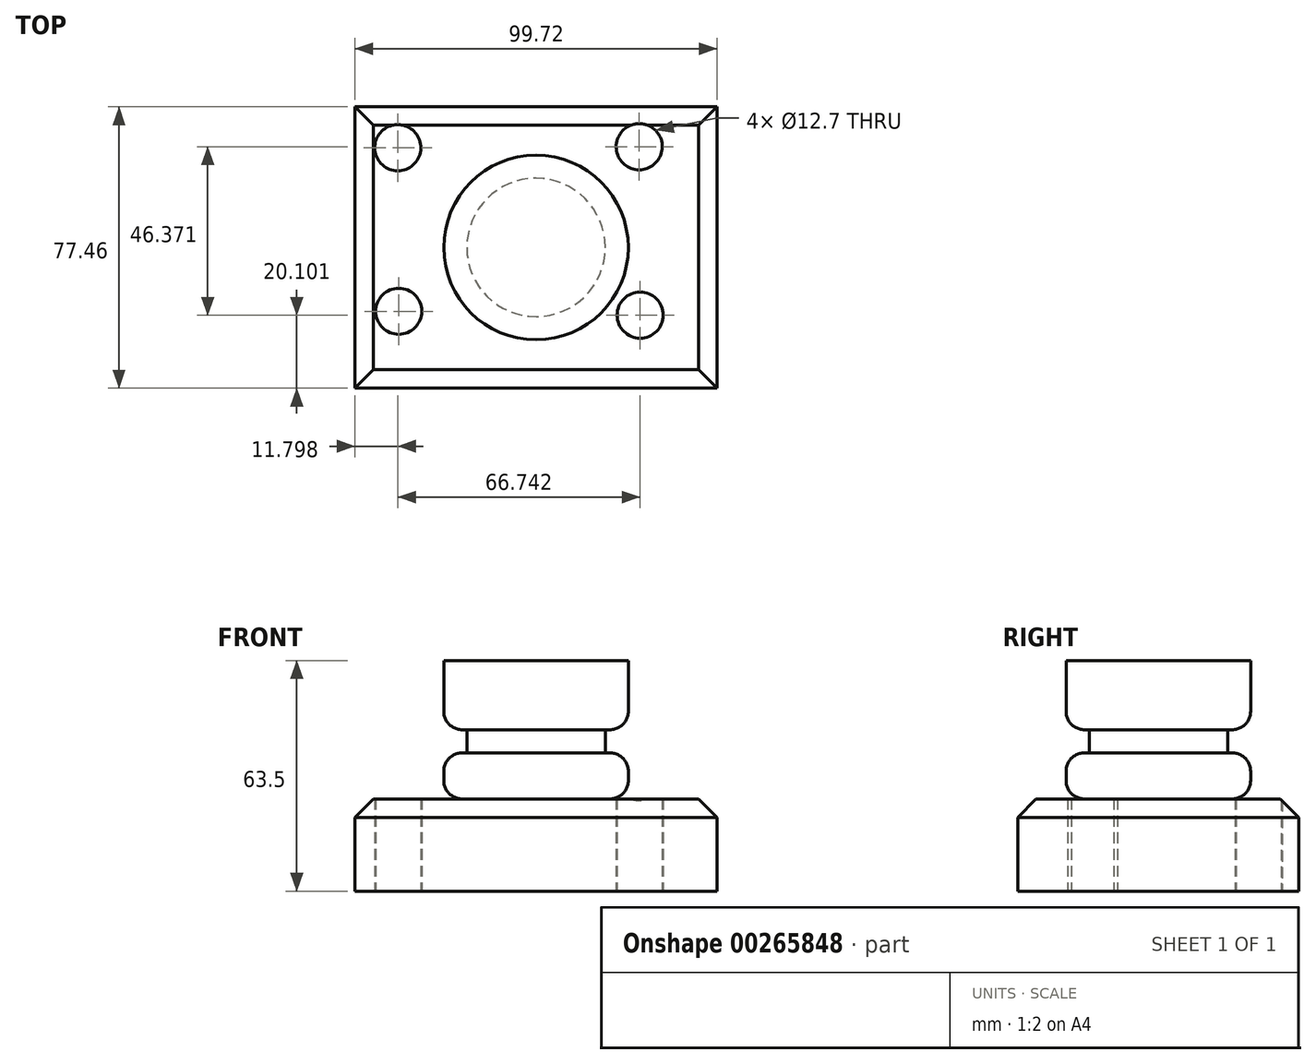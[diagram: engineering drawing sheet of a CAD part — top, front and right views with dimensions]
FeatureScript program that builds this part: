
annotation { "Feature Type Name" : "Feature", "Feature Type Description" : "" }
export const myFeature = defineFeature(function(context is Context, id is Id, definition is map)
    precondition{}
    {
        {
            var Q0;
            Q0=qCreatedBy(makeId("Top.planeOp"),FACE);
            var sketch = newSketch(context, id + "F0", { "sketchPlane" : qUnion([Q0])});
            skCircle(sketch, "E0", {"center": v(-38.06, 27.47) * mm, "radius": 6.35 * mm});
            skCircle(sketch, "E1", {"center": v(28.41, 27.74) * mm, "radius": 6.35 * mm});
            skCircle(sketch, "E2", {"center": v(-37.8, -17.56) * mm, "radius": 6.35 * mm});
            skCircle(sketch, "E3", {"center": v(28.68, -18.63) * mm, "radius": 6.35 * mm});
            skLineSegment(sketch, "E4.bottom", {"start": v(-49.86, 38.73) * mm, "end": v(49.86, 38.73) * mm});
            skLineSegment(sketch, "E4.top", {"start": v(-49.86, -38.73) * mm, "end": v(49.86, -38.73) * mm});
            skLineSegment(sketch, "E4.left", {"start": v(-49.86, 38.73) * mm, "end": v(-49.86, -38.73) * mm});
            skLineSegment(sketch, "E4.right", {"start": v(49.86, 38.73) * mm, "end": v(49.86, -38.73) * mm});
            skPoint(sketch, "E4.middle", {"position": v(0, 0) * mm});
            skSolve(sketch);
        }
        {
            var Q0;
            Q0 = qSketchRegion(id + "F0", true);
            extrude(context, id + "F1", {"entities" : qUnion([Q0]), "depth" : 25.4 * mm});
        }
        {
            var Q0;
            Q0=qCreatedBy(makeId("Right.planeOp"),FACE);
            var sketch = newSketch(context, id + "F2", { "sketchPlane" : qUnion([Q0])});
            skLineSegment(sketch, "E5.bottom", {"start": v(-25.4, 63.5) * mm, "end": v(0, 63.5) * mm});
            skLineSegment(sketch, "E5.top", {"start": v(-25.4, 25.4) * mm, "end": v(0, 25.4) * mm});
            skLineSegment(sketch, "E5.left", {"start": v(-25.4, 63.5) * mm, "end": v(-25.4, 25.4) * mm});
            skLineSegment(sketch, "E5.right", {"start": v(0, 63.5) * mm, "end": v(0, 25.4) * mm});
            skSolve(sketch);
        }
        {
            var Q0;
            Q0=makeQuery(id+"F2.imprint","IMPRINT",FACE,{"disambiguationData":[TD([[makeQuery(id+"F2.imprint","IMPRINT",EDGE,{"derivedFrom":sQuery(id+"F2.wireOp",EDGE,"E5.bottom")}),-1.0]])]});
            var Q1;
            Q1=sQuery(id+"F2.wireOp",EDGE,"E5.right");
            revolve(context, id + "F3", {"entities" : qUnion([Q0]), "axis" : qUnion([Q1]), "revolveType" : RevolveType.FULL});
        }
        {
            var Q0;
            Q0=qCreatedBy(makeId("Right.planeOp"),FACE);
            var sketch = newSketch(context, id + "F4", { "sketchPlane" : qUnion([Q0])});
            skLineSegment(sketch, "E6.bottom", {"start": v(-37.37, 38.1) * mm, "end": v(-19.05, 38.1) * mm});
            skLineSegment(sketch, "E6.top", {"start": v(-37.37, 44.45) * mm, "end": v(-19.05, 44.45) * mm});
            skLineSegment(sketch, "E6.left", {"start": v(-37.37, 38.1) * mm, "end": v(-37.37, 44.45) * mm});
            skLineSegment(sketch, "E6.right", {"start": v(-19.05, 38.1) * mm, "end": v(-19.05, 44.45) * mm});
            skPoint(sketch, "E6.middle", {"position": v(-28.21, 41.28) * mm});
            skSolve(sketch);
        }
        {
            var Q0;
            Q0 = qSketchRegion(id + "F4", true);
            var Q1;
            Q1=makeQuery(id+"F3.opRevolve","SWEPT_FACE",FACE,{"disambiguationData":[OSD([sQuery(id+"F2.wireOp",EDGE,"E5.left")])]});
            revolve(context, id + "F5", {"operationType" : NewBodyOperationType.REMOVE, "entities" : qUnion([Q0]), "axis" : qUnion([Q1]), "revolveType" : RevolveType.FULL, "oppositeDirection" : true});
        }
        {
            var Q0;
            Q0=makeQuery(id+"F1.opExtrude","CAP_EDGE",EDGE,{"disambiguationData":[OSD([sQuery(id+"F0.wireOp",EDGE,"E4.right")])],"isStart":false});
            var Q1;
            Q1=makeQuery(id+"F1.opExtrude","CAP_EDGE",EDGE,{"disambiguationData":[OSD([sQuery(id+"F0.wireOp",EDGE,"E4.bottom")])],"isStart":false});
            var Q2;
            Q2=makeQuery(id+"F1.opExtrude","CAP_EDGE",EDGE,{"disambiguationData":[OSD([sQuery(id+"F0.wireOp",EDGE,"E4.left")])],"isStart":false});
            var Q3;
            Q3=makeQuery(id+"F1.opExtrude","CAP_EDGE",EDGE,{"disambiguationData":[OSD([sQuery(id+"F0.wireOp",EDGE,"E4.top")])],"isStart":false});
            chamfer(context, id + "F6", {"entities" : qUnion([Q0, Q1, Q2, Q3]), "width" : 5.08 * mm, "tangentPropagation" : true});
        }
        {
            var Q0;
            Q0=makeQuery(id+"F5.boolean.opBoolean","INTERSECT",EDGE,{"derivedFrom":[makeQuery(id+"F3.opRevolve","SWEPT_FACE",FACE,{"disambiguationData":[OSD([sQuery(id+"F2.wireOp",EDGE,"E5.left")])]}),makeQuery(id+"F5.opRevolve","SWEPT_FACE",FACE,{"disambiguationData":[OSD([sQuery(id+"F4.wireOp",EDGE,"E6.bottom")])]})]});
            var Q1;
            Q1=makeQuery(id+"F5.boolean.opBoolean","INTERSECT",EDGE,{"derivedFrom":[makeQuery(id+"F3.opRevolve","SWEPT_FACE",FACE,{"disambiguationData":[OSD([sQuery(id+"F2.wireOp",EDGE,"E5.left")])]}),makeQuery(id+"F5.opRevolve","SWEPT_FACE",FACE,{"disambiguationData":[OSD([sQuery(id+"F4.wireOp",EDGE,"E6.top")])]})]});
            fillet(context, id + "F7", {"entities" : qUnion([Q0, Q1]), "radius" : 5.08 * mm, "tangentPropagation" : true, "allowEdgeOverflow" : false});
        }
        {
            var Q0;
            Q0=makeQuery(id+"F3.opRevolve","SWEPT_EDGE",EDGE,{"disambiguationData":[OSD([sQuery(id+"F2.wireOp",EDGE,"E5.top"),sQuery(id+"F2.wireOp",EDGE,"E5.left")])]});
            fillet(context, id + "F8", {"entities" : qUnion([Q0]), "radius" : 5.08 * mm, "tangentPropagation" : true, "allowEdgeOverflow" : false});
        }
    });
